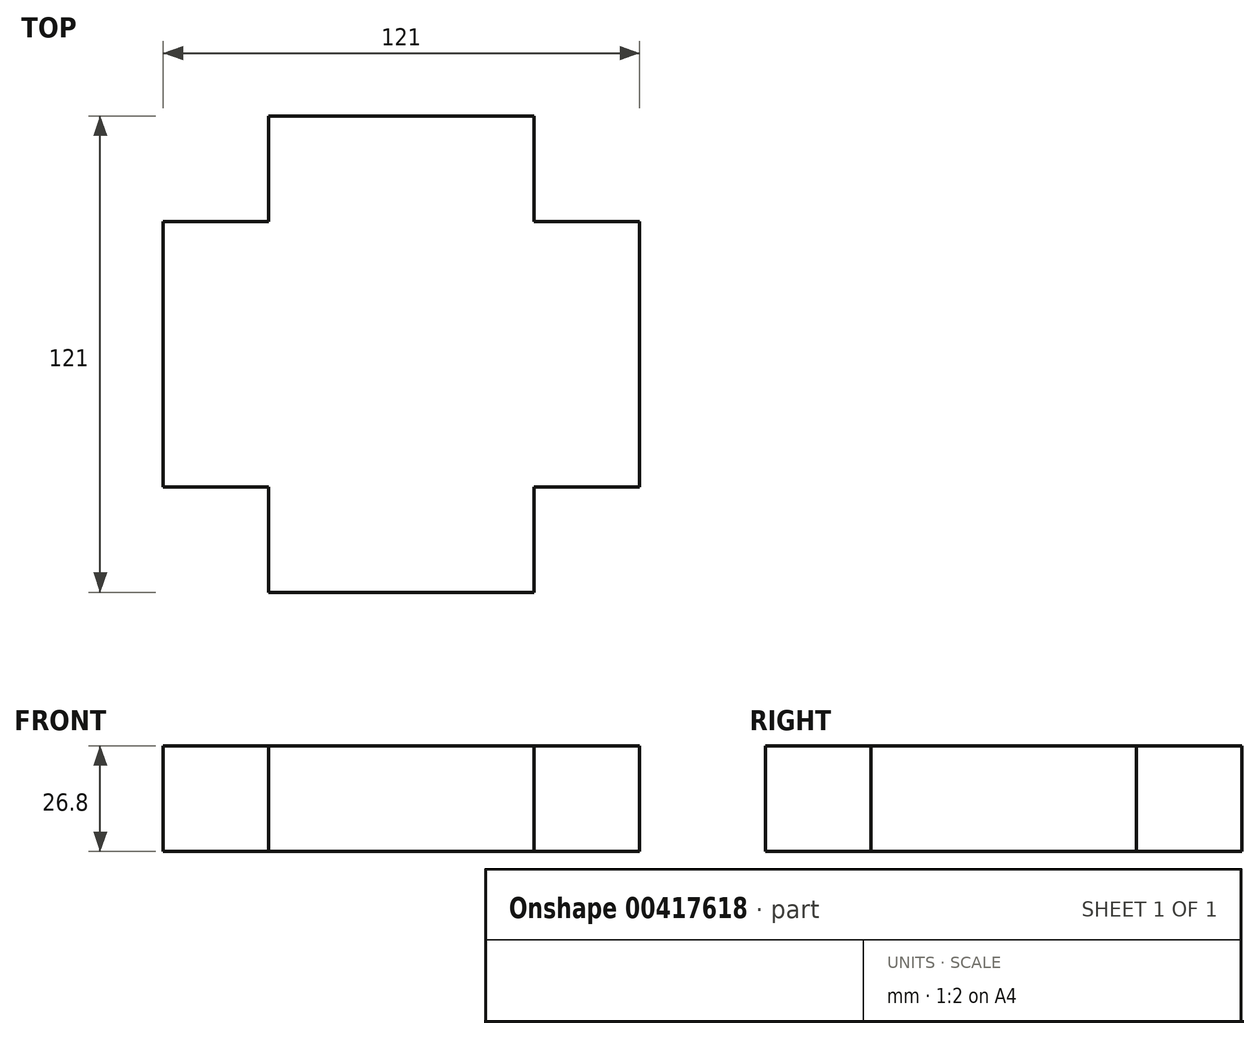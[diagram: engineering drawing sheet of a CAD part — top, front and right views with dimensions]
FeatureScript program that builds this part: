
annotation { "Feature Type Name" : "Feature", "Feature Type Description" : "" }
export const myFeature = defineFeature(function(context is Context, id is Id, definition is map)
    precondition{}
    {
        {
            var Q0;
            Q0=qCreatedBy(makeId("Top.planeOp"),FACE);
            var sketch = newSketch(context, id + "F0", { "sketchPlane" : qUnion([Q0])});
            skLineSegment(sketch, "E0.bottom", {"start": v(-38.33, 39.37) * mm, "end": v(55.87, 39.37) * mm});
            skLineSegment(sketch, "E0.top", {"start": v(-38.33, -81.63) * mm, "end": v(82.67, -81.63) * mm});
            skLineSegment(sketch, "E0.left", {"start": v(-38.33, 39.37) * mm, "end": v(-38.33, -81.63) * mm});
            skLineSegment(sketch, "E0.right", {"start": v(82.67, 39.37) * mm, "end": v(82.67, -81.63) * mm});
            skLineSegment(sketch, "E1.top", {"start": v(-38.33, 12.57) * mm, "end": v(-11.53, 12.57) * mm});
            skLineSegment(sketch, "E1.right", {"start": v(-11.53, 39.37) * mm, "end": v(-11.53, 12.57) * mm});
            skLineSegment(sketch, "E2.top", {"start": v(-38.33, -54.83) * mm, "end": v(-11.53, -54.83) * mm});
            skLineSegment(sketch, "E2.right", {"start": v(-11.53, -81.63) * mm, "end": v(-11.53, -54.83) * mm});
            skLineSegment(sketch, "E3.top", {"start": v(82.67, -54.83) * mm, "end": v(55.87, -54.83) * mm});
            skLineSegment(sketch, "E3.right", {"start": v(55.87, -81.63) * mm, "end": v(55.87, -54.83) * mm});
            skLineSegment(sketch, "E4.bottom", {"start": v(82.67, 39.37) * mm, "end": v(55.87, 39.37) * mm});
            skLineSegment(sketch, "E4.top", {"start": v(82.67, 12.57) * mm, "end": v(55.87, 12.57) * mm});
            skLineSegment(sketch, "E4.right", {"start": v(55.87, 39.37) * mm, "end": v(55.87, 12.57) * mm});
            skSolve(sketch);
        }
        {
            var Q0;
            {var subQ3=sQuery(id+"F0.wireOp",EDGE,"E1.top");Q0=makeQuery(id+"F0.imprint","IMPRINT",FACE,{"disambiguationData":[TD([[makeQuery(id+"F0.imprint","IMPRINT",EDGE,{"derivedFrom":subQ3}),-1.0]])]});}
            extrude(context, id + "F1", {"entities" : qUnion([Q0]), "depth" : 26.8 * mm});
        }
    });
